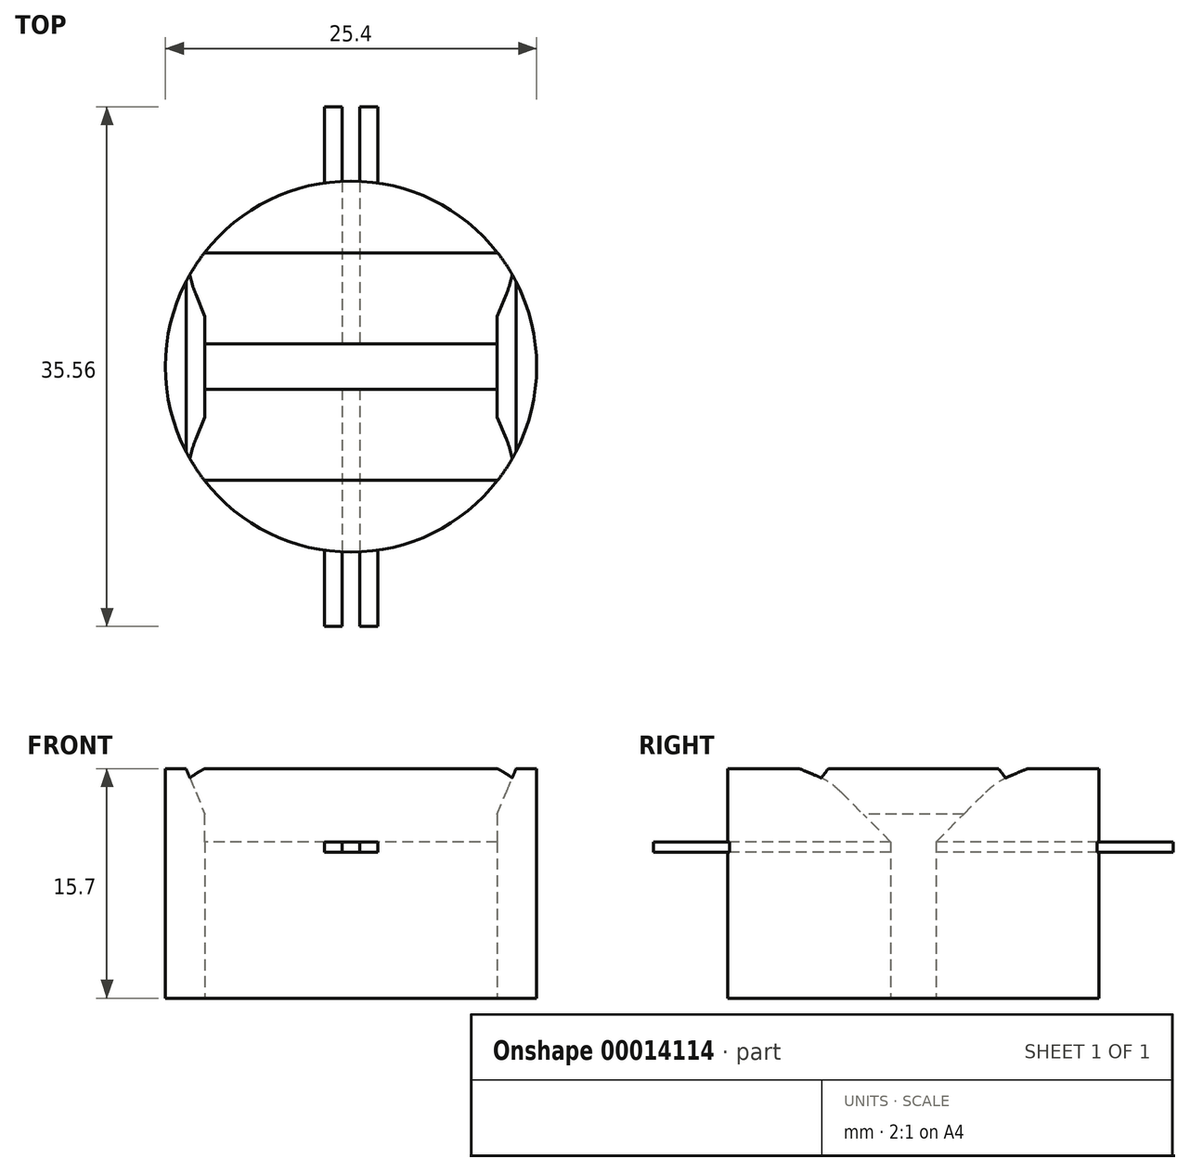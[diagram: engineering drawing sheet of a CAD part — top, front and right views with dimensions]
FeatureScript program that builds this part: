
annotation { "Feature Type Name" : "Feature", "Feature Type Description" : "" }
export const myFeature = defineFeature(function(context is Context, id is Id, definition is map)
    precondition{}
    {
        {
            var Q0;
            Q0=qCreatedBy(makeId("Top.planeOp"),FACE);
            var sketch = newSketch(context, id + "F0", { "sketchPlane" : qUnion([Q0])});
            skCircle(sketch, "E0", {"center": v(0, 0) * mm, "radius": 12.7 * mm});
            skLineSegment(sketch, "E1.rect.bottom", {"start": v(-10, 1.55) * mm, "end": v(10, 1.55) * mm});
            skLineSegment(sketch, "E1.rect.top", {"start": v(-10, -1.55) * mm, "end": v(10, -1.55) * mm});
            skLineSegment(sketch, "E1.rect.left", {"start": v(-10, 1.55) * mm, "end": v(-10, -1.55) * mm});
            skLineSegment(sketch, "E1.rect.right", {"start": v(10, 1.55) * mm, "end": v(10, -1.55) * mm});
            skSolve(sketch);
        }
        {
            var Q0;
            Q0=makeQuery(id+"F0.imprint","IMPRINT",FACE,{"disambiguationData":[TD([[makeQuery(id+"F0.imprint","IMPRINT",EDGE,{"derivedFrom":sQuery(id+"F0.wireOp",EDGE,"E0")}),1.0]])]});
            extrude(context, id + "F1", {"entities" : qUnion([Q0]), "depth" : 10 * mm});
        }
        {
            var Q0;
            Q0=makeQuery(id+"F1.opExtrude","CAP_FACE",FACE,{"disambiguationData":[OSD([sQuery(id+"F0.wireOp",EDGE,"E0"),sQuery(id+"F0.wireOp",EDGE,"E1.rect.bottom"),sQuery(id+"F0.wireOp",EDGE,"E1.rect.top"),sQuery(id+"F0.wireOp",EDGE,"E1.rect.left"),sQuery(id+"F0.wireOp",EDGE,"E1.rect.right")])],"isStart":false});
            var sketch = newSketch(context, id + "F2", { "sketchPlane" : qUnion([Q0])});
            skCircle(sketch, "E2", {"center": v(0, 0) * mm, "radius": 12.7 * mm});
            skLineSegment(sketch, "E3.rect.bottom", {"start": v(-10, -1.55) * mm, "end": v(10, -1.55) * mm});
            skLineSegment(sketch, "E3.rect.top", {"start": v(-10, 1.55) * mm, "end": v(10, 1.55) * mm});
            skLineSegment(sketch, "E3.rect.left", {"start": v(-10, -1.55) * mm, "end": v(-10, 1.55) * mm});
            skLineSegment(sketch, "E3.rect.right", {"start": v(10, -1.55) * mm, "end": v(10, 1.55) * mm});
            skLineSegment(sketch, "E4.rect.bottom", {"start": v(-0.6, 17.78) * mm, "end": v(0.6, 17.78) * mm});
            skLineSegment(sketch, "E4.rect.top", {"start": v(-0.6, -17.78) * mm, "end": v(0.6, -17.78) * mm});
            skLineSegment(sketch, "E4.rect.left", {"start": v(-0.6, 17.78) * mm, "end": v(-0.6, -17.78) * mm});
            skLineSegment(sketch, "E4.rect.right", {"start": v(0.6, 17.78) * mm, "end": v(0.6, -17.78) * mm});
            skLineSegment(sketch, "E5.rect.bottom", {"start": v(-1.83, 17.78) * mm, "end": v(1.83, 17.78) * mm});
            skLineSegment(sketch, "E5.rect.top", {"start": v(-1.83, -17.78) * mm, "end": v(1.83, -17.78) * mm});
            skLineSegment(sketch, "E5.rect.left", {"start": v(-1.83, 17.78) * mm, "end": v(-1.83, -17.78) * mm});
            skLineSegment(sketch, "E5.rect.right", {"start": v(1.83, 17.78) * mm, "end": v(1.83, -17.78) * mm});
            skSolve(sketch);
        }
        {
            var Q0;
            {var subQ0=sQuery(id+"F2.wireOp",EDGE,"E5.rect.left");var subQ1=sQuery(id+"F2.wireOp",EDGE,"E2");var subQ2=makeQuery(id+"F2.imprint","INTERSECT",VERTEX,{"disambiguationData":[OD(0.0)],"derivedFrom":[subQ1,subQ0]});Q0=makeQuery(id+"F2.imprint","IMPRINT",FACE,{"disambiguationData":[TD([[makeQuery(id+"F2.imprint","IMPRINT",EDGE,{"disambiguationData":[TD([[subQ2,1.0]])],"derivedFrom":subQ1}),-1.0]])]});}
            var Q1;
            {var subQ0=sQuery(id+"F2.wireOp",EDGE,"E5.rect.left");var subQ1=sQuery(id+"F2.wireOp",EDGE,"E2");var subQ2=makeQuery(id+"F2.imprint","INTERSECT",VERTEX,{"disambiguationData":[OD(1.0)],"derivedFrom":[subQ1,subQ0]});Q1=makeQuery(id+"F2.imprint","IMPRINT",FACE,{"disambiguationData":[TD([[makeQuery(id+"F2.imprint","IMPRINT",EDGE,{"disambiguationData":[TD([[subQ2,-1.0]])],"derivedFrom":subQ1}),-1.0]])]});}
            var Q2;
            {var subQ8=sQuery(id+"F2.wireOp",EDGE,"E3.rect.right");Q2=makeQuery(id+"F2.imprint","IMPRINT",FACE,{"disambiguationData":[TD([[makeQuery(id+"F2.imprint","IMPRINT",EDGE,{"derivedFrom":subQ8}),1.0]])]});}
            var Q3;
            {var subQ8=sQuery(id+"F2.wireOp",EDGE,"E3.rect.left");Q3=makeQuery(id+"F2.imprint","IMPRINT",FACE,{"disambiguationData":[TD([[makeQuery(id+"F2.imprint","IMPRINT",EDGE,{"derivedFrom":subQ8}),-1.0]])]});}
            var Q4;
            {var subQ0=sQuery(id+"F2.wireOp",EDGE,"E5.rect.right");var subQ1=sQuery(id+"F2.wireOp",EDGE,"E2");var subQ2=makeQuery(id+"F2.imprint","INTERSECT",VERTEX,{"disambiguationData":[OD(1.0)],"derivedFrom":[subQ1,subQ0]});Q4=makeQuery(id+"F2.imprint","IMPRINT",FACE,{"disambiguationData":[TD([[makeQuery(id+"F2.imprint","IMPRINT",EDGE,{"disambiguationData":[TD([[subQ2,1.0]])],"derivedFrom":subQ1}),-1.0]])]});}
            var Q5;
            {var subQ0=sQuery(id+"F2.wireOp",EDGE,"E5.rect.right");var subQ3=sQuery(id+"F2.wireOp",EDGE,"E2");var subQ4=makeQuery(id+"F2.imprint","INTERSECT",VERTEX,{"disambiguationData":[OD(0.0)],"derivedFrom":[subQ3,subQ0]});Q5=makeQuery(id+"F2.imprint","IMPRINT",FACE,{"disambiguationData":[TD([[makeQuery(id+"F2.imprint","IMPRINT",EDGE,{"disambiguationData":[TD([[subQ4,-1.0]])],"derivedFrom":subQ3}),1.0]])]});}
            var Q6;
            {var subQ0=sQuery(id+"F2.wireOp",EDGE,"E5.rect.right");var subQ3=sQuery(id+"F2.wireOp",EDGE,"E2");var subQ4=makeQuery(id+"F2.imprint","INTERSECT",VERTEX,{"disambiguationData":[OD(1.0)],"derivedFrom":[subQ3,subQ0]});Q6=makeQuery(id+"F2.imprint","IMPRINT",FACE,{"disambiguationData":[TD([[makeQuery(id+"F2.imprint","IMPRINT",EDGE,{"disambiguationData":[TD([[subQ4,1.0]])],"derivedFrom":subQ3}),1.0]])]});}
            var Q7;
            {var subQ0=sQuery(id+"F2.wireOp",EDGE,"E5.rect.left");var subQ3=sQuery(id+"F2.wireOp",EDGE,"E2");var subQ4=makeQuery(id+"F2.imprint","INTERSECT",VERTEX,{"disambiguationData":[OD(1.0)],"derivedFrom":[subQ3,subQ0]});Q7=makeQuery(id+"F2.imprint","IMPRINT",FACE,{"disambiguationData":[TD([[makeQuery(id+"F2.imprint","IMPRINT",EDGE,{"disambiguationData":[TD([[subQ4,-1.0]])],"derivedFrom":subQ3}),1.0]])]});}
            var Q8;
            {var subQ0=sQuery(id+"F2.wireOp",EDGE,"E5.rect.left");var subQ3=sQuery(id+"F2.wireOp",EDGE,"E2");var subQ4=makeQuery(id+"F2.imprint","INTERSECT",VERTEX,{"disambiguationData":[OD(0.0)],"derivedFrom":[subQ3,subQ0]});Q8=makeQuery(id+"F2.imprint","IMPRINT",FACE,{"disambiguationData":[TD([[makeQuery(id+"F2.imprint","IMPRINT",EDGE,{"disambiguationData":[TD([[subQ4,1.0]])],"derivedFrom":subQ3}),1.0]])]});}
            var Q9;
            {var subQ0=sQuery(id+"F2.wireOp",EDGE,"E5.rect.right");var subQ1=sQuery(id+"F2.wireOp",EDGE,"E2");var subQ2=makeQuery(id+"F2.imprint","INTERSECT",VERTEX,{"disambiguationData":[OD(0.0)],"derivedFrom":[subQ1,subQ0]});Q9=makeQuery(id+"F2.imprint","IMPRINT",FACE,{"disambiguationData":[TD([[makeQuery(id+"F2.imprint","IMPRINT",EDGE,{"disambiguationData":[TD([[subQ2,-1.0]])],"derivedFrom":subQ1}),-1.0]])]});}
            extrude(context, id + "F3", {"entities" : qUnion([Q0, Q1, Q2, Q3, Q4, Q5, Q6, Q7, Q8, Q9]), "operationType" : NewBodyOperationType.ADD, "depth" : .7 * mm});
        }
        {
            var Q0;
            Q0=makeQuery(id+"F3.opExtrude","CAP_FACE",FACE,{"disambiguationData":[OSD([sQuery(id+"F2.wireOp",EDGE,"E2"),sQuery(id+"F2.wireOp",EDGE,"E3.rect.bottom"),sQuery(id+"F2.wireOp",EDGE,"E3.rect.top"),sQuery(id+"F2.wireOp",EDGE,"E3.rect.left"),sQuery(id+"F2.wireOp",EDGE,"E4.rect.left"),sQuery(id+"F2.wireOp",EDGE,"E5.rect.bottom"),sQuery(id+"F2.wireOp",EDGE,"E5.rect.top"),sQuery(id+"F2.wireOp",EDGE,"E5.rect.left")])],"isStart":false});
            var sketch = newSketch(context, id + "F4", { "sketchPlane" : qUnion([Q0])});
            skCircle(sketch, "E6", {"center": v(0, 0) * mm, "radius": 12.7 * mm});
            skLineSegment(sketch, "E7.rect.bottom", {"start": v(10, 1.55) * mm, "end": v(-10, 1.55) * mm});
            skLineSegment(sketch, "E7.rect.top", {"start": v(10, -1.55) * mm, "end": v(-10, -1.55) * mm});
            skLineSegment(sketch, "E7.rect.left", {"start": v(10, 1.55) * mm, "end": v(10, -1.55) * mm});
            skLineSegment(sketch, "E7.rect.right", {"start": v(-10, 1.55) * mm, "end": v(-10, -1.55) * mm});
            skSolve(sketch);
        }
        {
            var Q0;
            {var subQ15=sQuery(id+"F4.wireOp",EDGE,"E7.rect.right");Q0=makeQuery(id+"F4.imprint","IMPRINT",FACE,{"disambiguationData":[TD([[makeQuery(id+"F4.imprint","IMPRINT",EDGE,{"derivedFrom":subQ15}),-1.0]])]});}
            var Q1;
            {var subQ13=sQuery(id+"F4.wireOp",EDGE,"E7.rect.left");Q1=makeQuery(id+"F4.imprint","IMPRINT",FACE,{"disambiguationData":[TD([[makeQuery(id+"F4.imprint","IMPRINT",EDGE,{"derivedFrom":subQ13}),1.0]])]});}
            extrude(context, id + "F5", {"entities" : qUnion([Q0, Q1]), "operationType" : NewBodyOperationType.ADD, "depth" : 5 * mm});
        }
        {
            var Q0;
            Q0=makeQuery(id+"F5.opExtrude","CAP_EDGE",EDGE,{"disambiguationData":[OSD([sQuery(id+"F4.wireOp",EDGE,"E7.rect.bottom")])],"isStart":false});
            var Q1;
            Q1=makeQuery(id+"F5.opExtrude","CAP_EDGE",EDGE,{"disambiguationData":[OSD([sQuery(id+"F4.wireOp",EDGE,"E7.rect.top")])],"isStart":false});
            chamfer(context, id + "F6", {"entities" : qUnion([Q0, Q1]), "width" : 5 * mm, "tangentPropagation" : true});
        }
        {
            var Q0;
            Q0=makeQuery(id+"F5.opExtrude","CAP_EDGE",EDGE,{"disambiguationData":[OSD([sQuery(id+"F4.wireOp",EDGE,"E7.rect.right")])],"isStart":false});
            var Q1;
            Q1=makeQuery(id+"F5.opExtrude","CAP_EDGE",EDGE,{"disambiguationData":[OSD([sQuery(id+"F4.wireOp",EDGE,"E7.rect.left")])],"isStart":false});
            chamfer(context, id + "F7", {"entities" : qUnion([Q0, Q1]), "width" : 1 * mm, "tangentPropagation" : true});
        }
        {
            var Q0;
            {var subQ0=sQuery(id+"F4.wireOp",EDGE,"E7.rect.top");Q0=makeQuery(id+"F6.opChamfer","BLEND_EDGE",EDGE,{"blendedFrom":[makeQuery(id+"F5.opExtrude","CAP_EDGE",EDGE,{"disambiguationData":[OSD([subQ0])],"isStart":false}),makeQuery(id+"F5.opExtrude","CAP_FACE",FACE,{"disambiguationData":[OSD([sQuery(id+"F4.wireOp",EDGE,"E6"),sQuery(id+"F4.wireOp",EDGE,"E7.rect.bottom"),subQ0,sQuery(id+"F4.wireOp",EDGE,"E7.rect.left"),sQuery(id+"F4.wireOp",EDGE,"E7.rect.right")])],"isStart":false})],"blendedInto":[makeQuery(id+"F5.opExtrude","CAP_FACE",FACE,{"disambiguationData":[OSD([sQuery(id+"F4.wireOp",EDGE,"E6"),sQuery(id+"F4.wireOp",EDGE,"E7.rect.bottom"),subQ0,sQuery(id+"F4.wireOp",EDGE,"E7.rect.left"),sQuery(id+"F4.wireOp",EDGE,"E7.rect.right")])],"isStart":false})]});}
            var Q1;
            {var subQ0=sQuery(id+"F4.wireOp",EDGE,"E7.rect.bottom");Q1=makeQuery(id+"F6.opChamfer","BLEND_EDGE",EDGE,{"blendedFrom":[makeQuery(id+"F5.opExtrude","CAP_EDGE",EDGE,{"disambiguationData":[OSD([subQ0])],"isStart":false}),makeQuery(id+"F5.opExtrude","CAP_FACE",FACE,{"disambiguationData":[OSD([sQuery(id+"F4.wireOp",EDGE,"E6"),subQ0,sQuery(id+"F4.wireOp",EDGE,"E7.rect.top"),sQuery(id+"F4.wireOp",EDGE,"E7.rect.left"),sQuery(id+"F4.wireOp",EDGE,"E7.rect.right")])],"isStart":false})],"blendedInto":[makeQuery(id+"F5.opExtrude","CAP_FACE",FACE,{"disambiguationData":[OSD([sQuery(id+"F4.wireOp",EDGE,"E6"),subQ0,sQuery(id+"F4.wireOp",EDGE,"E7.rect.top"),sQuery(id+"F4.wireOp",EDGE,"E7.rect.left"),sQuery(id+"F4.wireOp",EDGE,"E7.rect.right")])],"isStart":false})]});}
            chamfer(context, id + "F8", {"entities" : qUnion([Q0, Q1]), "width" : 3 * mm, "tangentPropagation" : true});
        }
        {
            var Q0;
            {var subQ0=sQuery(id+"F4.wireOp",EDGE,"E7.rect.top");Q0=makeQuery(id+"F8.opChamfer","BLEND_EDGE",EDGE,{"blendedFrom":[makeQuery(id+"F6.opChamfer","BLEND_EDGE",EDGE,{"blendedFrom":[makeQuery(id+"F5.opExtrude","CAP_EDGE",EDGE,{"disambiguationData":[OSD([subQ0])],"isStart":false}),makeQuery(id+"F5.opExtrude","CAP_FACE",FACE,{"disambiguationData":[OSD([sQuery(id+"F4.wireOp",EDGE,"E6"),sQuery(id+"F4.wireOp",EDGE,"E7.rect.bottom"),subQ0,sQuery(id+"F4.wireOp",EDGE,"E7.rect.left"),sQuery(id+"F4.wireOp",EDGE,"E7.rect.right")])],"isStart":false})],"blendedInto":[makeQuery(id+"F5.opExtrude","CAP_FACE",FACE,{"disambiguationData":[OSD([sQuery(id+"F4.wireOp",EDGE,"E6"),sQuery(id+"F4.wireOp",EDGE,"E7.rect.bottom"),subQ0,sQuery(id+"F4.wireOp",EDGE,"E7.rect.left"),sQuery(id+"F4.wireOp",EDGE,"E7.rect.right")])],"isStart":false})]}),makeQuery(id+"F6.opChamfer","BLEND_FACE",FACE,{"disambiguationData":[OSD([subQ0])]})],"blendedInto":[makeQuery(id+"F6.opChamfer","BLEND_FACE",FACE,{"disambiguationData":[OSD([subQ0])]})]});}
            var Q1;
            {var subQ0=sQuery(id+"F4.wireOp",EDGE,"E7.rect.bottom");Q1=makeQuery(id+"F8.opChamfer","BLEND_EDGE",EDGE,{"blendedFrom":[makeQuery(id+"F6.opChamfer","BLEND_EDGE",EDGE,{"blendedFrom":[makeQuery(id+"F5.opExtrude","CAP_EDGE",EDGE,{"disambiguationData":[OSD([subQ0])],"isStart":false}),makeQuery(id+"F5.opExtrude","CAP_FACE",FACE,{"disambiguationData":[OSD([sQuery(id+"F4.wireOp",EDGE,"E6"),subQ0,sQuery(id+"F4.wireOp",EDGE,"E7.rect.top"),sQuery(id+"F4.wireOp",EDGE,"E7.rect.left"),sQuery(id+"F4.wireOp",EDGE,"E7.rect.right")])],"isStart":false})],"blendedInto":[makeQuery(id+"F5.opExtrude","CAP_FACE",FACE,{"disambiguationData":[OSD([sQuery(id+"F4.wireOp",EDGE,"E6"),subQ0,sQuery(id+"F4.wireOp",EDGE,"E7.rect.top"),sQuery(id+"F4.wireOp",EDGE,"E7.rect.left"),sQuery(id+"F4.wireOp",EDGE,"E7.rect.right")])],"isStart":false})]}),makeQuery(id+"F6.opChamfer","BLEND_FACE",FACE,{"disambiguationData":[OSD([subQ0])]})],"blendedInto":[makeQuery(id+"F6.opChamfer","BLEND_FACE",FACE,{"disambiguationData":[OSD([subQ0])]})]});}
            fillet(context, id + "F9", {"entities" : qUnion([Q0, Q1]), "radius" : 5.08 * mm, "tangentPropagation" : true, "allowEdgeOverflow" : false});
        }
        {
            var Q0;
            {var subQ0=sQuery(id+"F4.wireOp",EDGE,"E7.rect.right");Q0=makeQuery(id+"F7.opChamfer","BLEND_EDGE",EDGE,{"blendedFrom":[makeQuery(id+"F5.opExtrude","CAP_EDGE",EDGE,{"disambiguationData":[OSD([subQ0])],"isStart":false}),makeQuery(id+"F5.boolean.opBoolean","MERGE",FACE,{"derivedFrom":[makeQuery(id+"F3.boolean.opBoolean","MERGE",FACE,{"derivedFrom":[makeQuery(id+"F1.opExtrude","SWEPT_FACE",FACE,{"disambiguationData":[OSD([sQuery(id+"F0.wireOp",EDGE,"E1.rect.left")])]}),makeQuery(id+"F3.opExtrude","SWEPT_FACE",FACE,{"disambiguationData":[OSD([sQuery(id+"F2.wireOp",EDGE,"E3.rect.left")])]})]}),makeQuery(id+"F5.opExtrude","SWEPT_FACE",FACE,{"disambiguationData":[OSD([subQ0])]})]})],"blendedInto":[makeQuery(id+"F5.boolean.opBoolean","MERGE",FACE,{"derivedFrom":[makeQuery(id+"F3.boolean.opBoolean","MERGE",FACE,{"derivedFrom":[makeQuery(id+"F1.opExtrude","SWEPT_FACE",FACE,{"disambiguationData":[OSD([sQuery(id+"F0.wireOp",EDGE,"E1.rect.left")])]}),makeQuery(id+"F3.opExtrude","SWEPT_FACE",FACE,{"disambiguationData":[OSD([sQuery(id+"F2.wireOp",EDGE,"E3.rect.left")])]})]}),makeQuery(id+"F5.opExtrude","SWEPT_FACE",FACE,{"disambiguationData":[OSD([subQ0])]})]})]});}
            var Q1;
            {var subQ0=sQuery(id+"F4.wireOp",EDGE,"E7.rect.left");Q1=makeQuery(id+"F7.opChamfer","BLEND_EDGE",EDGE,{"blendedFrom":[makeQuery(id+"F5.opExtrude","CAP_EDGE",EDGE,{"disambiguationData":[OSD([subQ0])],"isStart":false}),makeQuery(id+"F5.boolean.opBoolean","MERGE",FACE,{"derivedFrom":[makeQuery(id+"F3.boolean.opBoolean","MERGE",FACE,{"derivedFrom":[makeQuery(id+"F1.opExtrude","SWEPT_FACE",FACE,{"disambiguationData":[OSD([sQuery(id+"F0.wireOp",EDGE,"E1.rect.right")])]}),makeQuery(id+"F3.opExtrude","SWEPT_FACE",FACE,{"disambiguationData":[OSD([sQuery(id+"F2.wireOp",EDGE,"E3.rect.right")])]})]}),makeQuery(id+"F5.opExtrude","SWEPT_FACE",FACE,{"disambiguationData":[OSD([subQ0])]})]})],"blendedInto":[makeQuery(id+"F5.boolean.opBoolean","MERGE",FACE,{"derivedFrom":[makeQuery(id+"F3.boolean.opBoolean","MERGE",FACE,{"derivedFrom":[makeQuery(id+"F1.opExtrude","SWEPT_FACE",FACE,{"disambiguationData":[OSD([sQuery(id+"F0.wireOp",EDGE,"E1.rect.right")])]}),makeQuery(id+"F3.opExtrude","SWEPT_FACE",FACE,{"disambiguationData":[OSD([sQuery(id+"F2.wireOp",EDGE,"E3.rect.right")])]})]}),makeQuery(id+"F5.opExtrude","SWEPT_FACE",FACE,{"disambiguationData":[OSD([subQ0])]})]})]});}
            chamfer(context, id + "F10", {"entities" : qUnion([Q0, Q1]), "width" : 5.08 * mm, "tangentPropagation" : true});
        }
    });
